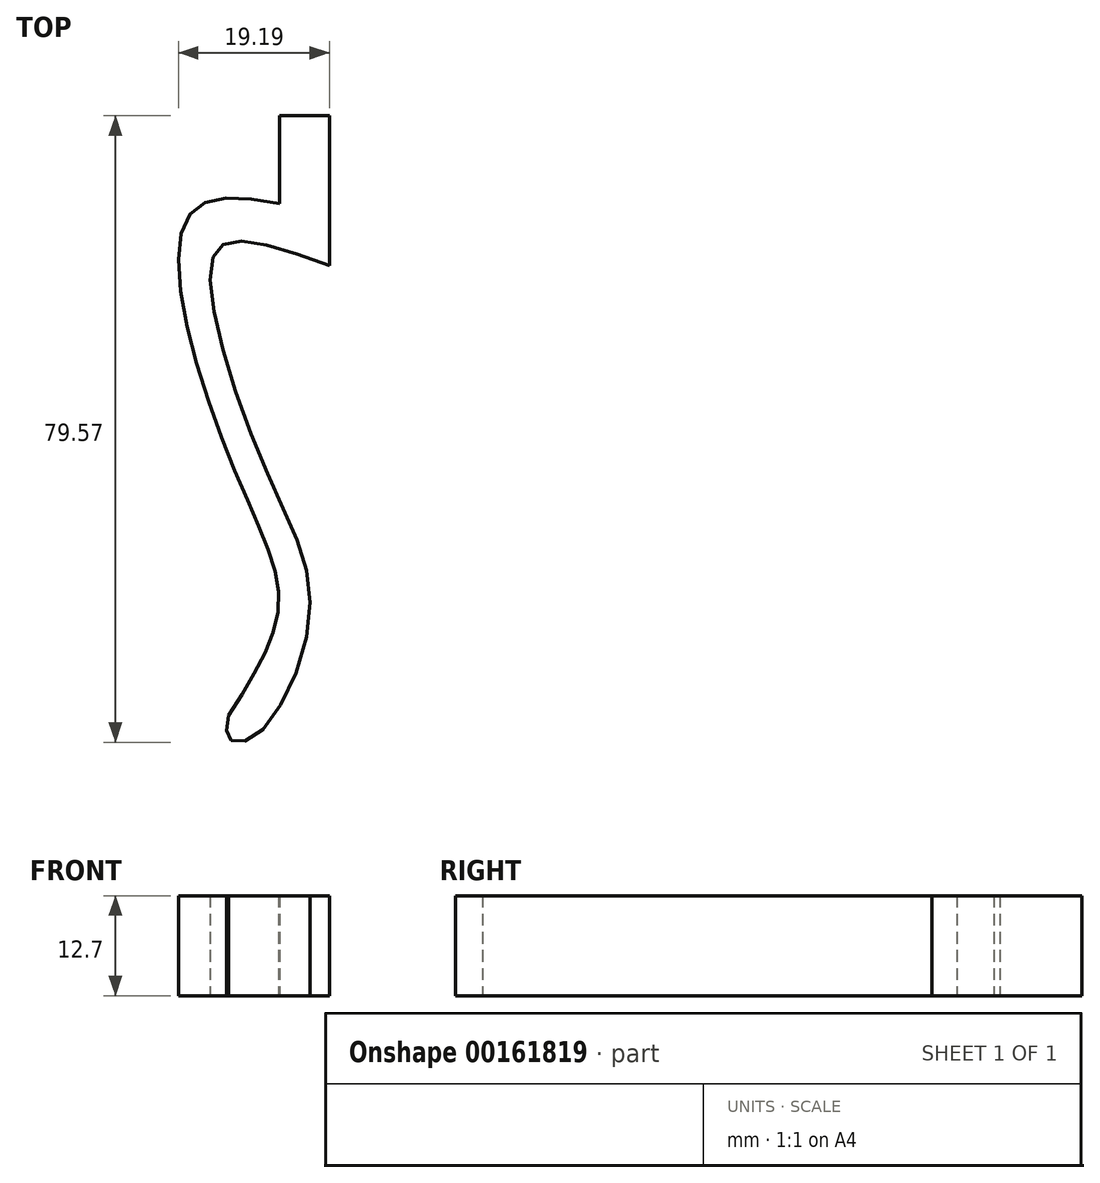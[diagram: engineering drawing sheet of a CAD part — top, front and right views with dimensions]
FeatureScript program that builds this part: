
annotation { "Feature Type Name" : "Feature", "Feature Type Description" : "" }
export const myFeature = defineFeature(function(context is Context, id is Id, definition is map)
    precondition{}
    {
        {
            var Q0;
            Q0=qCreatedBy(makeId("Top.planeOp"),FACE);
            var sketch = newSketch(context, id + "F0", { "sketchPlane" : qUnion([Q0])});
            skLineSegment(sketch, "E0", {"start": v(0, 0) * mm, "end": v(0, 6.35) * mm});
            skFitSpline(sketch, "E1", {"points": [v(0, 6.35) * mm, v(-17.88, 6.35) * mm, v(-12.44, -25.06) * mm, v(-6.47, -43.17) * mm, v(-12.8, -57.11) * mm], "startDerivative": vector(-97.3, 25.25) * mm, "endDerivative": vector(-41.9, -65.27) * mm});
            skFitSpline(sketch, "E2", {"points": [v(-12.8, -57.11) * mm, v(-12.8, -60) * mm, v(-9.55, -59.83) * mm, v(-2.49, -44.07) * mm, v(-7.92, -26.33) * mm, v(-15.16, -1.34) * mm, v(-12.8, 3) * mm, v(0, 0) * mm], "startDerivative": vector(-9.88, -45.89) * mm, "endDerivative": vector(96.23, -35.4) * mm});
            skSolve(sketch);
        }
        {
            var Q0;
            Q0 = qSketchRegion(id + "F0", true);
            extrude(context, id + "F1", {"entities" : qUnion([Q0]), "depth" : 12.7 * mm});
        }
        {
            var Q0;
            Q0=makeQuery(id+"F1.opExtrude","SWEPT_FACE",FACE,{"disambiguationData":[OSD([sQuery(id+"F0.wireOp",EDGE,"E0")])]});
            var sketch = newSketch(context, id + "F2", { "sketchPlane" : qUnion([Q0])});
            skLineSegment(sketch, "E3", {"start": v(6.35, 12.7) * mm, "end": v(19.05, 12.7) * mm});
            skLineSegment(sketch, "E4", {"start": v(19.05, 12.7) * mm, "end": v(19.05, 0) * mm});
            skLineSegment(sketch, "E5", {"start": v(19.05, 0) * mm, "end": v(6.35, 0) * mm});
            skLineSegment(sketch, "E6", {"start": v(6.35, 0) * mm, "end": v(6.35, 12.7) * mm});
            skSolve(sketch);
        }
        {
            var Q0;
            Q0 = qSketchRegion(id + "F2", true);
            extrude(context, id + "F3", {"entities" : qUnion([Q0]), "operationType" : NewBodyOperationType.ADD, "oppositeDirection" : true, "depth" : 6.35 * mm});
        }
    });
